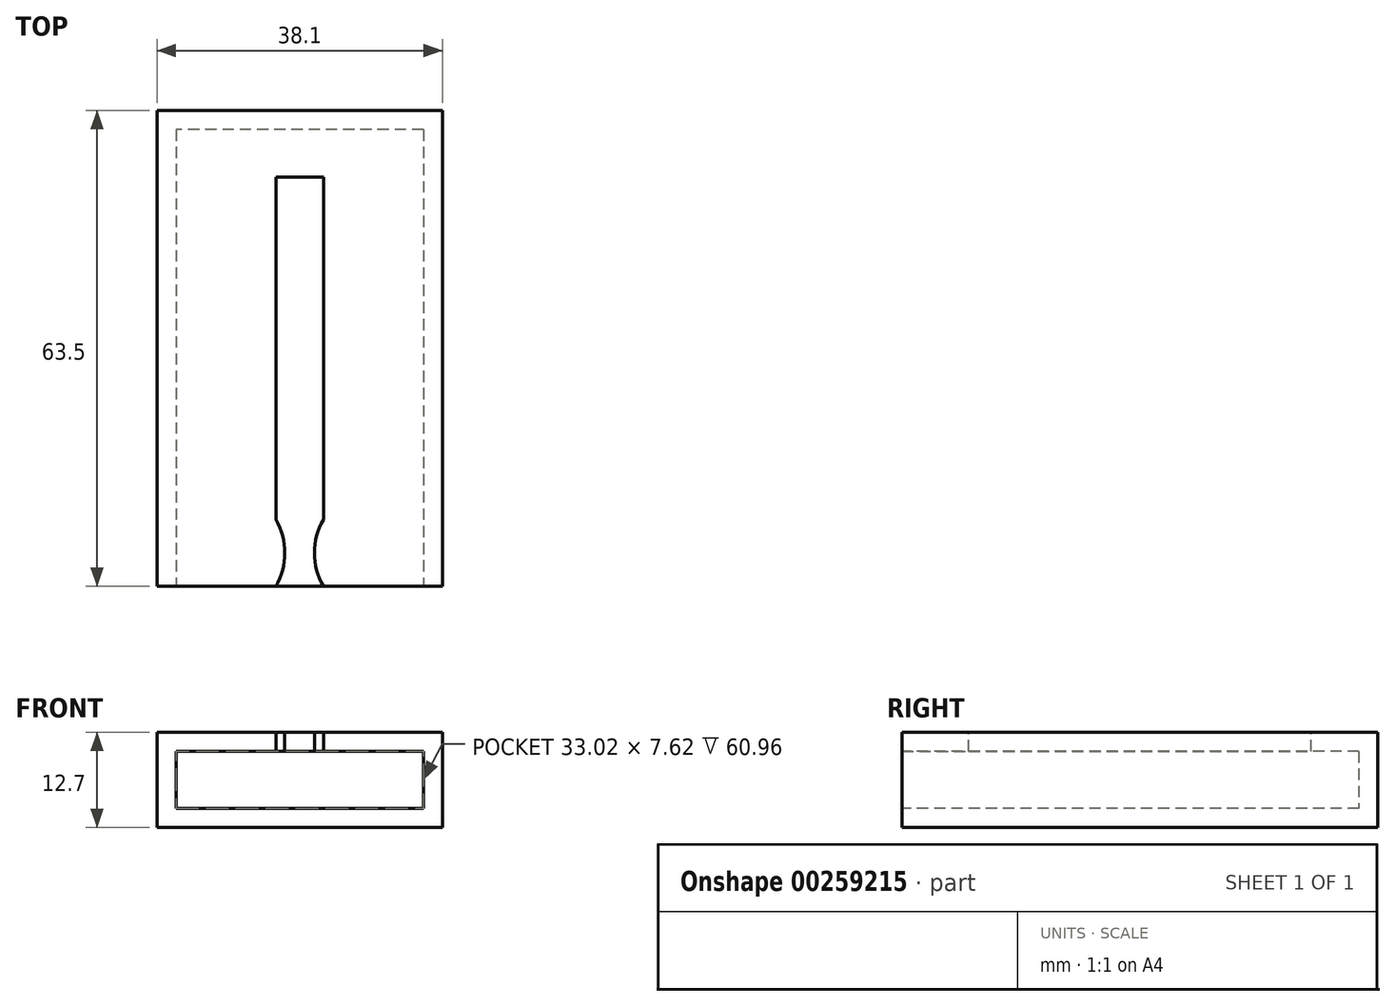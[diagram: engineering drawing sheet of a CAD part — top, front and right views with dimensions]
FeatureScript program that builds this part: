
annotation { "Feature Type Name" : "Feature", "Feature Type Description" : "" }
export const myFeature = defineFeature(function(context is Context, id is Id, definition is map)
    precondition{}
    {
        {
            var Q0;
            Q0=qCreatedBy(makeId("Top.planeOp"),FACE);
            var sketch = newSketch(context, id + "F0", { "sketchPlane" : qUnion([Q0])});
            skLineSegment(sketch, "E0.bottom", {"start": v(19.05, 31.75) * mm, "end": v(-19.05, 31.75) * mm});
            skLineSegment(sketch, "E0.top", {"start": v(19.05, -31.75) * mm, "end": v(-19.05, -31.75) * mm});
            skLineSegment(sketch, "E0.left", {"start": v(19.05, 31.75) * mm, "end": v(19.05, -31.75) * mm});
            skLineSegment(sketch, "E0.right", {"start": v(-19.05, 31.75) * mm, "end": v(-19.05, -31.75) * mm});
            skPoint(sketch, "E0.middle", {"position": v(0, 0) * mm});
            skSolve(sketch);
        }
        {
            var Q0;
            Q0=makeQuery(id+"F0.imprint","IMPRINT",FACE,{"disambiguationData":[TD([[makeQuery(id+"F0.imprint","IMPRINT",EDGE,{"derivedFrom":sQuery(id+"F0.wireOp",EDGE,"E0.bottom")}),1.0]])]});
            extrude(context, id + "F1", {"entities" : qUnion([Q0]), "depth" : 12.7 * mm});
        }
        {
            var Q0;
            Q0=makeQuery(id+"F1.opExtrude","SWEPT_FACE",FACE,{"disambiguationData":[OSD([sQuery(id+"F0.wireOp",EDGE,"E0.top")])]});
            shell(context, id + "F2", {"entities" : qUnion([Q0]), "thickness" : 2.54 * mm});
        }
        {
            var Q0;
            Q0=makeQuery(id+"F1.opExtrude","CAP_FACE",FACE,{"disambiguationData":[OSD([sQuery(id+"F0.wireOp",EDGE,"E0.bottom"),sQuery(id+"F0.wireOp",EDGE,"E0.top"),sQuery(id+"F0.wireOp",EDGE,"E0.left"),sQuery(id+"F0.wireOp",EDGE,"E0.right")])],"isStart":false});
            var sketch = newSketch(context, id + "F3", { "sketchPlane" : qUnion([Q0])});
            skLineSegment(sketch, "E1.bottom", {"start": v(3.18, 22.86) * mm, "end": v(-3.17, 22.86) * mm});
            skLineSegment(sketch, "E1.left", {"start": v(3.18, 22.86) * mm, "end": v(3.17, -22.86) * mm});
            skLineSegment(sketch, "E1.right", {"start": v(-3.17, 22.86) * mm, "end": v(-3.18, -22.86) * mm});
            skPoint(sketch, "E1.middle", {"position": v(0, 0) * mm});
            skLineSegment(sketch, "E2.left", {"start": v(-3.18, -22.86) * mm, "end": v(-3.18, -22.86) * mm});
            skLineSegment(sketch, "E2.right", {"start": v(3.17, -22.86) * mm, "end": v(3.17, -22.86) * mm});
            skLineSegment(sketch, "E3.bottom", {"start": v(-3.18, -31.75) * mm, "end": v(3.17, -31.75) * mm});
            skLineSegment(sketch, "E3.top", {"start": v(-3.18, -22.86) * mm, "end": v(3.17, -22.86) * mm});
            skLineSegment(sketch, "E3.left", {"start": v(-3.18, -31.75) * mm, "end": v(-3.18, -22.86) * mm});
            skLineSegment(sketch, "E3.right", {"start": v(3.17, -31.75) * mm, "end": v(3.17, -22.86) * mm});
            skArc(sketch, "E4", {"start": v(-3.18, -31.75) * mm, "mid": v(-1.98, -27.3) * mm, "end": v(-3.18, -22.86) * mm});
            skArc(sketch, "E5", {"start": v(3.17, -22.86) * mm, "mid": v(1.98, -27.3) * mm, "end": v(3.17, -31.75) * mm});
            skSolve(sketch);
        }
        {
            var Q0;
            Q0=makeQuery(id+"F3.imprint","IMPRINT",FACE,{"disambiguationData":[TD([[makeQuery(id+"F3.imprint","IMPRINT",EDGE,{"derivedFrom":sQuery(id+"F3.wireOp",EDGE,"E1.bottom")}),1.0]])]});
            var Q1;
            Q1=makeQuery(id+"F3.imprint","IMPRINT",FACE,{"disambiguationData":[TD([[makeQuery(id+"F3.imprint","IMPRINT",EDGE,{"derivedFrom":sQuery(id+"F3.wireOp",EDGE,"E3.bottom")}),-1.0]])]});
            extrude(context, id + "F4", {"entities" : qUnion([Q0, Q1]), "operationType" : NewBodyOperationType.REMOVE, "endBound" : BoundingType.UP_TO_NEXT, "oppositeDirection" : true, "depth" : 25.4 * mm});
        }
    });
